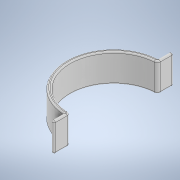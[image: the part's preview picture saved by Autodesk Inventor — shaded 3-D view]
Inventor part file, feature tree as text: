
AUTODESK INVENTOR PART (.ipt)
format: ipt  version: 2020 (Build 240168000, 168)  size: 185,344 bytes
history: native  units: in
note: dims shown in document units (in); Inventor stores cm internally (conversion verified against a paired STEP export)
features: fillet x3, extrude x1, sketch x1
ambient origin geometry x8: Origin, YZ Plane, XZ Plane, XY Plane, X Axis, Y Axis, Z Axis, Center Point
bodies: Solid1 (feature_tree)
feature tree (5):
  extrude  "Extrusion1"  Depth=0.0591in
  fillet  "Fillet1"  Radius=0.1575in
  fillet  "Fillet2"  Radius=0.5118in
  fillet  "Fillet3"  Radius=0.5118in
  sketch  "Sketch1"  dims[d0=3.937in d1=1.9685in d2=0.1575in d3=0.5118in d4=0.5118in d5=0.1181in d6=0.1181in d7=1.1811in d8=0.0in d9=0.125in d10=0.0591in d11=0.0591in]
